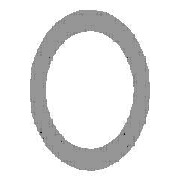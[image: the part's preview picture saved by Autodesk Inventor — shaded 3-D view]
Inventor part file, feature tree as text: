
AUTODESK INVENTOR PART (.ipt)
format: ipt  version: 2013 (Build 170138000, 138)  size: 138,240 bytes
history: native  units: mm (DEFAULTED — no unit token found)
features: plane x6, sketch x6, other x4, extrude x3
ambient origin geometry x8: Origin, YZ Plane, XZ Plane, XY Plane, X Axis, Y Axis, Z Axis, Center Point
bodies: Solid1 (feature_tree), Body (feature_tree)
feature tree (19):
  parser-record x1  (decoder bookkeeping rows leaked as tree rows — omitted from the tree; the rows remain in map.json)
  other  "Driven Length"
  other  "Start plane"
  other  "End plane"
  plane  "Work Plane4"
  plane  "Work Plane5"
  plane  "Work Plane6"
  extrude  "Extrusion2"  Depth=3.3782mm
  plane  "Work Plane9"
  extrude  "Extrusion3"  TaperAngle=0.0deg  [1 undecoded]
  plane  "Work Plane10"
  extrude  "Extrusion4"  TaperAngle=90.0deg  [1 undecoded]
  sketch  "Sketch"  dims[d10=25.4mm d11=0.0mm d12=6.35mm d13=25.4mm d14=0.0mm]
  sketch  "Sketch3"  dims[d0=33.401mm d1=3.3782mm]
  plane  "Work Plane3"
  sketch  "Sketch4"  dims[d2=800.1mm d3=0.0mm d4=-0.0mm]
  sketch  "Sketch5"  dims[d5=800.1mm d6=90.0deg]
  sketch  "Sketch6"  dims[d7=800.1mm]
  sketch  "Sketch7"  dims[d8=3.302mm d9=0.0mm]
note: 2 required parameter values undecoded (feature->parameter linkage not recoverable at this tier; creation-order binding heuristic only, values carry confidence <= 0.55)
